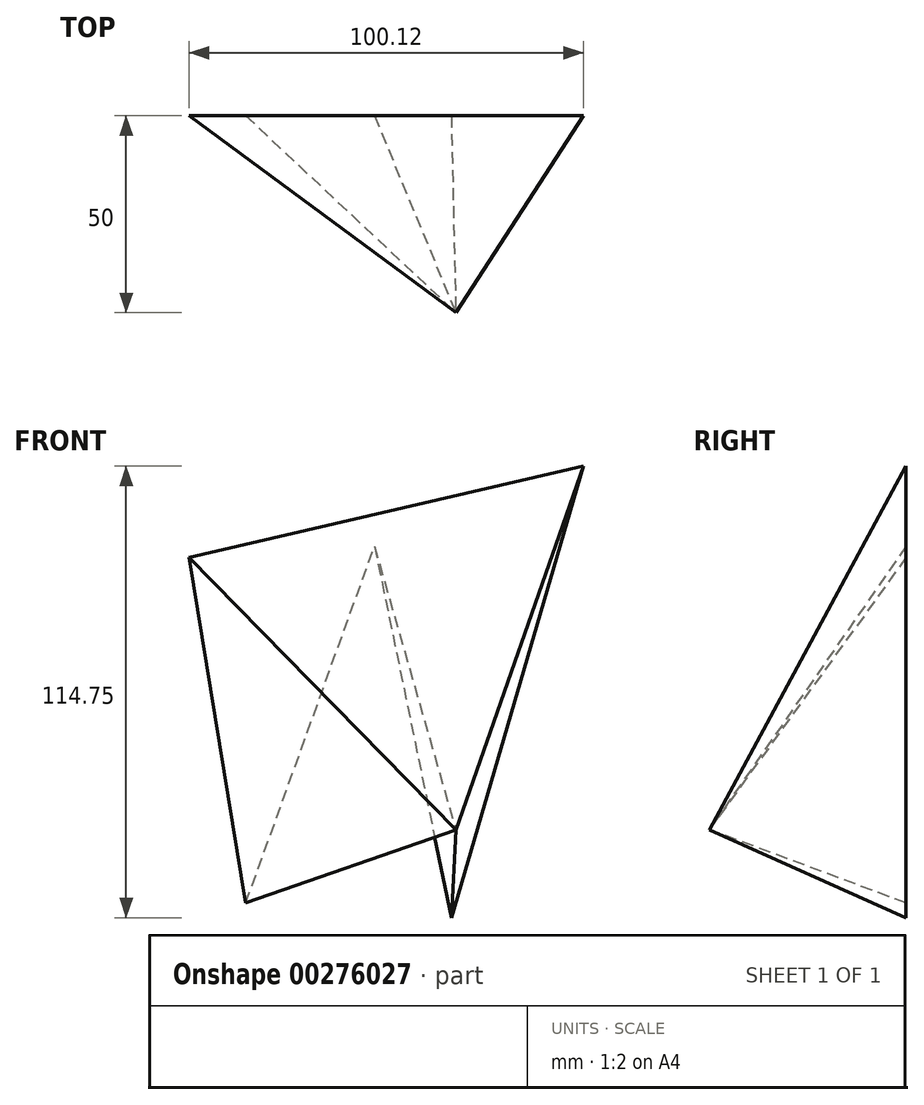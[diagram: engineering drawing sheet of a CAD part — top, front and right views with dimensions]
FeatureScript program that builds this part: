
annotation { "Feature Type Name" : "Feature", "Feature Type Description" : "" }
export const myFeature = defineFeature(function(context is Context, id is Id, definition is map)
    precondition{}
    {
        {
            var Q0;
            Q0=qCreatedBy(makeId("Front.planeOp"),FACE);
            var sketch = newSketch(context, id + "F0", { "sketchPlane" : qUnion([Q0])});
            skLineSegment(sketch, "E0", {"start": v(-51.35, 35.14) * mm, "end": v(-37, -52.64) * mm});
            skLineSegment(sketch, "E1", {"start": v(-37, -52.64) * mm, "end": v(-4.3, 38.01) * mm});
            skLineSegment(sketch, "E2", {"start": v(-4.3, 38.01) * mm, "end": v(15.2, -56.37) * mm});
            skLineSegment(sketch, "E3", {"start": v(15.2, -56.37) * mm, "end": v(48.77, 58.38) * mm});
            skLineSegment(sketch, "E4", {"start": v(48.77, 58.38) * mm, "end": v(-51.35, 35.14) * mm});
            skSolve(sketch);
        }
        {
            var Q0;
            Q0=qCreatedBy(makeId("Front.planeOp"),FACE);
            cPlane(context, id + "F1", {"entities" : qUnion([Q0]), "cplaneType" : CPlaneType.OFFSET, "offset" : 50 * mm, "width" : 150 * mm, "height" : 150 * mm});
        }
        {
            var Q0;
            Q0=qCreatedBy(id+"F1.planeOp",FACE);
            var sketch = newSketch(context, id + "F2", { "sketchPlane" : qUnion([Q0])});
            skPoint(sketch, "E5", {"position": v(16.35, -34) * mm});
            skSolve(sketch);
        }
        {
            var Q0;
            Q0=makeQuery(id+"F0.imprint","IMPRINT",FACE,{"disambiguationData":[TD([[makeQuery(id+"F0.imprint","IMPRINT",EDGE,{"derivedFrom":sQuery(id+"F0.wireOp",EDGE,"E0")}),1.0]])]});
            var Q1;
            Q1=sQuery(id+"F2.wireOp",VERTEX,"E5");
            loft(context, id + "F3", {"sheetProfilesArray" : [{ "sheetProfileEntities" : qUnion([Q0]) }, { "sheetProfileEntities" : qUnion([Q1]) }]});
        }
    });
